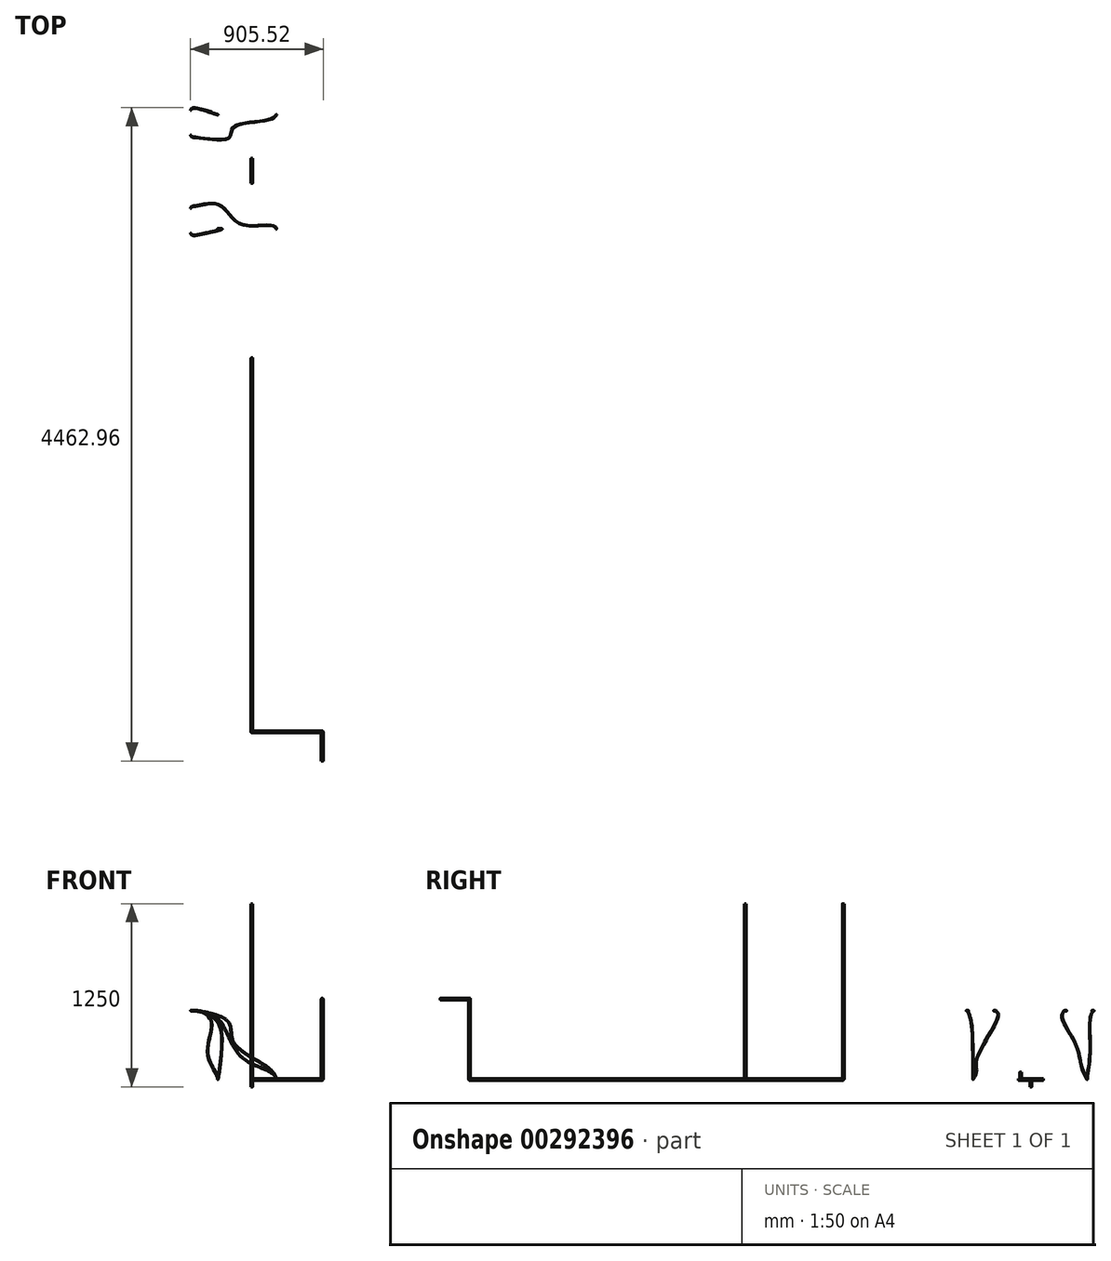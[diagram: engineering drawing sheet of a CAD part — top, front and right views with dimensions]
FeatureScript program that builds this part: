
annotation { "Feature Type Name" : "Feature", "Feature Type Description" : "" }
export const myFeature = defineFeature(function(context is Context, id is Id, definition is map)
    precondition{}
    {
        {
            var Q0;
            Q0=qCreatedBy(makeId("Front.planeOp"),FACE);
            var sketch = newSketch(context, id + "F0", { "sketchPlane" : qUnion([Q0])});
            skCircle(sketch, "E0", {"center": v(0, 0) * mm, "radius": 6.35 * mm});
            skSolve(sketch);
        }
        {
            var Q0;
            Q0 = qSketchRegion(id + "F0", true);
            extrude(context, id + "F1", {"entities" : qUnion([Q0]), "depth" : 2550 * mm});
        }
        {
            var Q0;
            Q0=qCreatedBy(makeId("Top.planeOp"),FACE);
            var sketch = newSketch(context, id + "F2", { "sketchPlane" : qUnion([Q0])});
            skLineSegment(sketch, "E1", {"start": v(0, 0) * mm, "end": v(0, -1880) * mm, "construction": true});
            skLineSegment(sketch, "E2", {"start": v(0, -1880) * mm, "end": v(0, -2550) * mm, "construction": true});
            skCircle(sketch, "E3", {"center": v(0, -1880) * mm, "radius": 6.35 * mm});
            skCircle(sketch, "E4", {"center": v(0, -2550) * mm, "radius": 6.35 * mm});
            skSolve(sketch);
        }
        {
            var Q0;
            Q0 = qSketchRegion(id + "F2", true);
            extrude(context, id + "F3", {"entities" : qUnion([Q0]), "operationType" : NewBodyOperationType.ADD, "depth" : 1200 * mm});
        }
        {
            var Q0;
            Q0=makeQuery(id+"F1.opExtrude","SWEPT_BODY",BODY,{"disambiguationData":[OSD([sQuery(id+"F0.wireOp",EDGE,"E0")])]});
            var Q1;
            Q1=makeQuery(id+"F3.opExtrude","SWEPT_FACE",FACE,{"disambiguationData":[OSD([sQuery(id+"F2.wireOp",EDGE,"E3")])]});
            transform(context, id + "F4", {"entities" : qUnion([Q0]), "transformType" : TransformType.ROTATION, "transformAxis" : qUnion([Q1]), "angle" : 180 * degree, "makeCopy" : false});
        }
        {
            var Q0;
            Q0=qCreatedBy(makeId("Top.planeOp"),FACE);
            var sketch = newSketch(context, id + "F5", { "sketchPlane" : qUnion([Q0])});
            skCircle(sketch, "E5", {"center": v(0, 0) * mm, "radius": 6.35 * mm});
            skSolve(sketch);
        }
        {
            var Q0;
            Q0 = qSketchRegion(id + "F5", true);
            extrude(context, id + "F6", {"entities" : qUnion([Q0]), "depth" : 50 * mm});
        }
        {
            var Q0;
            Q0=qCreatedBy(makeId("Top.planeOp"),FACE);
            var sketch = newSketch(context, id + "F7", { "sketchPlane" : qUnion([Q0])});
            skCircle(sketch, "E6", {"center": v(0, 71.05) * mm, "radius": 6.35 * mm});
            skLineSegment(sketch, "E7", {"start": v(0, 64.7) * mm, "end": v(0, 77.4) * mm, "construction": true});
            skLineSegment(sketch, "E8", {"start": v(-6.35, 71.05) * mm, "end": v(6.35, 71.05) * mm, "construction": true});
            skSolve(sketch);
        }
        {
            var Q0;
            Q0 = qSketchRegion(id + "F7", true);
            extrude(context, id + "F8", {"entities" : qUnion([Q0]), "oppositeDirection" : true, "depth" : 50 * mm});
        }
        {
            var Q0;
            Q0=sQuery(id+"F7.wireOp",EDGE,"E8");
            cPlane(context, id + "F9", {"entities" : qUnion([Q0]), "cplaneType" : CPlaneType.LINE_ANGLE, "offset" : 25 * mm, "angle" : 0 * degree, "width" : 150 * mm, "height" : 150 * mm});
        }
        {
            var Q0;
            Q0=qCreatedBy(id+"F9.planeOp",FACE);
            var sketch = newSketch(context, id + "F10", { "sketchPlane" : qUnion([Q0])});
            skCircle(sketch, "E9", {"center": v(0, 0) * mm, "radius": 6.35 * mm});
            skSolve(sketch);
        }
        {
            var Q0;
            Q0 = qSketchRegion(id + "F10", true);
            extrude(context, id + "F11", {"entities" : qUnion([Q0]), "operationType" : NewBodyOperationType.ADD, "endBound" : BoundingType.SYMMETRIC, "depth" : 170 * mm});
        }
        {
            var Q0;
            Q0=qCreatedBy(makeId("Top.planeOp"),FACE);
            cPlane(context, id + "F12", {"entities" : qUnion([Q0]), "cplaneType" : CPlaneType.OFFSET, "offset" : 470 * mm, "width" : 150 * mm, "height" : 150 * mm});
        }
        {
            var Q0;
            Q0=qCreatedBy(makeId("Top.planeOp"),FACE);
            var sketch = newSketch(context, id + "F13", { "sketchPlane" : qUnion([Q0])});
            skCircle(sketch, "E10", {"center": v(166.67, -325) * mm, "radius": 6.35 * mm});
            skCircle(sketch, "E11.0.1.0", {"center": v(166.67, 455) * mm, "radius": 6.35 * mm});
            skCircle(sketch, "E11.1.0.0", {"center": v(-233.33, -325) * mm, "radius": 6.35 * mm});
            skCircle(sketch, "E11.1.1.0", {"center": v(-233.33, 455) * mm, "radius": 6.35 * mm});
            skLineSegment(sketch, "E11.direction1", {"start": v(166.67, -325) * mm, "end": v(-233.33, -325) * mm, "construction": true});
            skLineSegment(sketch, "E11.direction2", {"start": v(166.67, -325) * mm, "end": v(166.67, 455) * mm, "construction": true});
            skSolve(sketch);
        }
        {
            var Q0;
            Q0=qCreatedBy(id+"F12.planeOp",FACE);
            var sketch = newSketch(context, id + "F14", { "sketchPlane" : qUnion([Q0])});
            skLineSegment(sketch, "E12", {"start": v(166.67, -325) * mm, "end": v(416.67, -325) * mm, "construction": true});
            skLineSegment(sketch, "E13", {"start": v(416.67, -354.52) * mm, "end": v(416.67, -325) * mm, "construction": true});
            skLineSegment(sketch, "E14", {"start": v(416.67, -354.52) * mm, "end": v(416.67, -269.52) * mm, "construction": true});
            skLineSegment(sketch, "E15", {"start": v(416.67, -269.52) * mm, "end": v(416.67, -184.52) * mm, "construction": true});
            skLineSegment(sketch, "E16", {"start": v(416.67, -184.52) * mm, "end": v(416.67, 400.48) * mm, "construction": true});
            skLineSegment(sketch, "E17", {"start": v(416.67, -325) * mm, "end": v(416.67, -384.52) * mm, "construction": true});
            skLineSegment(sketch, "E18", {"start": v(416.67, 400.48) * mm, "end": v(416.67, 315.48) * mm, "construction": true});
            skLineSegment(sketch, "E19", {"start": v(416.67, 400.48) * mm, "end": v(416.67, 485.48) * mm, "construction": true});
            skLineSegment(sketch, "E20.MirrorCS", {"start": v(-416.67, -354.52) * mm, "end": v(-416.67, -325) * mm, "construction": true});
            skLineSegment(sketch, "E21.MirrorCS", {"start": v(-416.67, -354.52) * mm, "end": v(-416.67, -269.52) * mm, "construction": true});
            skLineSegment(sketch, "E22.MirrorCS", {"start": v(-416.67, -325) * mm, "end": v(-416.67, -384.52) * mm, "construction": true});
            skLineSegment(sketch, "E23.MirrorCS", {"start": v(-166.67, -325) * mm, "end": v(-416.67, -325) * mm, "construction": true});
            skLineSegment(sketch, "E24.MirrorCS", {"start": v(-416.67, 400.48) * mm, "end": v(-416.67, 315.48) * mm, "construction": true});
            skLineSegment(sketch, "E25.MirrorCS", {"start": v(-416.67, 400.48) * mm, "end": v(-416.67, 485.48) * mm, "construction": true});
            skLineSegment(sketch, "E26.MirrorCS", {"start": v(-416.67, -269.52) * mm, "end": v(-416.67, -184.52) * mm, "construction": true});
            skLineSegment(sketch, "E27.MirrorCS", {"start": v(-416.67, -184.52) * mm, "end": v(-416.67, 400.48) * mm, "construction": true});
            skLineSegment(sketch, "E28", {"start": v(-416.67, -354.52) * mm, "end": v(-416.67, -369.52) * mm, "construction": true});
            skLineSegment(sketch, "E29", {"start": v(-416.67, -369.52) * mm, "end": v(-386.67, -369.52) * mm, "construction": true});
            skFitSpline(sketch, "E30", {"points": [v(-416.67, -354.52) * mm, v(-408.86, -366.73) * mm, v(-386.67, -369.52) * mm], "startDerivative": vector(0.34, -26.82) * mm, "endDerivative": vector(29.3, -3.47) * mm});
            skLineSegment(sketch, "E31", {"start": v(-416.67, -269.52) * mm, "end": v(-293.51, -269.52) * mm, "construction": true});
            skFitSpline(sketch, "E32.MirrorCS", {"points": [v(-416.67, -184.52) * mm, v(-408.86, -172.31) * mm, v(-386.67, -169.52) * mm], "startDerivative": vector(0.34, 26.82) * mm, "endDerivative": vector(29.3, 3.47) * mm});
            skLineSegment(sketch, "E33", {"start": v(-416.67, -184.52) * mm, "end": v(-416.67, 65.48) * mm, "construction": true});
            skLineSegment(sketch, "E34", {"start": v(-416.67, 65.48) * mm, "end": v(-295.06, 65.48) * mm, "construction": true});
            skFitSpline(sketch, "E35.MirrorCS", {"points": [v(-416.67, 315.48) * mm, v(-408.86, 303.27) * mm, v(-386.67, 300.48) * mm], "startDerivative": vector(0.34, -26.82) * mm, "endDerivative": vector(29.3, -3.47) * mm});
            skLineSegment(sketch, "E36", {"start": v(-416.67, 400.48) * mm, "end": v(-299.7, 400.48) * mm, "construction": true});
            skFitSpline(sketch, "E37.MirrorCS", {"points": [v(-416.67, 485.48) * mm, v(-408.86, 497.69) * mm, v(-386.67, 500.48) * mm], "startDerivative": vector(0.34, 26.82) * mm, "endDerivative": vector(29.3, 3.47) * mm});
            skLineSegment(sketch, "E38", {"start": v(-416.67, -354.52) * mm, "end": v(-309.5, -354.52) * mm});
            skLineSegment(sketch, "E39", {"start": v(-416.67, -184.52) * mm, "end": v(-206.18, -184.52) * mm});
            skLineSegment(sketch, "E40", {"start": v(-416.67, 315.48) * mm, "end": v(-297.33, 315.48) * mm});
            skLineSegment(sketch, "E41", {"start": v(-416.67, 485.48) * mm, "end": v(-294.97, 485.48) * mm});
            skSolve(sketch);
        }
        {
            var Q0;
            Q0=sQuery(id+"F14.wireOp",EDGE,"E38");
            cPlane(context, id + "F15", {"entities" : qUnion([Q0]), "cplaneType" : CPlaneType.LINE_ANGLE, "offset" : 25 * mm, "angle" : 0 * degree, "width" : 150 * mm, "height" : 150 * mm});
        }
        {
            var Q0;
            Q0=qCreatedBy(id+"F15.planeOp",FACE);
            var sketch = newSketch(context, id + "F16", { "sketchPlane" : qUnion([Q0])});
            skCircle(sketch, "E42", {"center": v(416.67, 470) * mm, "radius": 2.5 * mm});
            skSolve(sketch);
        }
        {
            var Q0;
            Q0=sQuery(id+"F14.wireOp",EDGE,"E39");
            cPlane(context, id + "F17", {"entities" : qUnion([Q0]), "cplaneType" : CPlaneType.LINE_ANGLE, "offset" : 25 * mm, "angle" : 0 * degree, "width" : 150 * mm, "height" : 150 * mm});
        }
        {
            var Q0;
            Q0=qCreatedBy(id+"F17.planeOp",FACE);
            var sketch = newSketch(context, id + "F18", { "sketchPlane" : qUnion([Q0])});
            skCircle(sketch, "E43", {"center": v(416.67, 470) * mm, "radius": 2.5 * mm});
            skSolve(sketch);
        }
        {
            var Q0;
            Q0=sQuery(id+"F14.wireOp",EDGE,"E40");
            cPlane(context, id + "F19", {"entities" : qUnion([Q0]), "cplaneType" : CPlaneType.LINE_ANGLE, "offset" : 25 * mm, "angle" : 0 * degree, "width" : 150 * mm, "height" : 150 * mm});
        }
        {
            var Q0;
            Q0=qCreatedBy(id+"F19.planeOp",FACE);
            var sketch = newSketch(context, id + "F20", { "sketchPlane" : qUnion([Q0])});
            skCircle(sketch, "E44", {"center": v(416.67, 470) * mm, "radius": 2.5 * mm});
            skSolve(sketch);
        }
        {
            var Q0;
            Q0=sQuery(id+"F14.wireOp",EDGE,"E41");
            cPlane(context, id + "F21", {"entities" : qUnion([Q0]), "cplaneType" : CPlaneType.LINE_ANGLE, "offset" : 25 * mm, "angle" : 0 * degree, "width" : 150 * mm, "height" : 150 * mm});
        }
        {
            var Q0;
            Q0=qCreatedBy(id+"F21.planeOp",FACE);
            var sketch = newSketch(context, id + "F22", { "sketchPlane" : qUnion([Q0])});
            skCircle(sketch, "E45", {"center": v(416.67, 470) * mm, "radius": 2.5 * mm});
            skSolve(sketch);
        }
        {
            var Q0;
            Q0=makeQuery(id+"F22.imprint","IMPRINT",FACE,{"disambiguationData":[TD([[makeQuery(id+"F22.imprint","IMPRINT",EDGE,{"derivedFrom":sQuery(id+"F22.wireOp",EDGE,"E45")}),1.0]])]});
            var Q1;
            Q1=sQuery(id+"F14.wireOp",EDGE,"E37.MirrorCS");
            sweep(context, id + "F23", {"profiles" : qUnion([Q0]), "path" : qUnion([Q1])});
        }
        {
            var Q0;
            Q0=makeQuery(id+"F20.imprint","IMPRINT",FACE,{"disambiguationData":[TD([[makeQuery(id+"F20.imprint","IMPRINT",EDGE,{"derivedFrom":sQuery(id+"F20.wireOp",EDGE,"E44")}),1.0]])]});
            var Q1;
            Q1=sQuery(id+"F20.wireOp",EDGE,"E44");
            var Q2;
            Q2=sQuery(id+"F14.wireOp",EDGE,"E35.MirrorCS");
            sweep(context, id + "F24", {"profiles" : qUnion([Q0]), "surfaceProfiles" : qUnion([Q1]), "path" : qUnion([Q2])});
        }
        {
            var Q0;
            Q0=makeQuery(id+"F18.imprint","IMPRINT",FACE,{"disambiguationData":[TD([[makeQuery(id+"F18.imprint","IMPRINT",EDGE,{"derivedFrom":sQuery(id+"F18.wireOp",EDGE,"E43")}),1.0]])]});
            var Q1;
            Q1=sQuery(id+"F14.wireOp",EDGE,"E32.MirrorCS");
            sweep(context, id + "F25", {"profiles" : qUnion([Q0]), "path" : qUnion([Q1])});
        }
        {
            var Q0;
            Q0=makeQuery(id+"F16.imprint","IMPRINT",FACE,{"disambiguationData":[TD([[makeQuery(id+"F16.imprint","IMPRINT",EDGE,{"derivedFrom":sQuery(id+"F16.wireOp",EDGE,"E42")}),1.0]])]});
            var Q1;
            Q1=sQuery(id+"F16.wireOp",EDGE,"E42");
            var Q2;
            Q2=sQuery(id+"F14.wireOp",EDGE,"E30");
            sweep(context, id + "F26", {"profiles" : qUnion([Q0]), "surfaceProfiles" : qUnion([Q1]), "path" : qUnion([Q2])});
        }
        {
            var Q0;
            Q0=sQuery(id+"F14.wireOp",VERTEX,"E29.end");
            var Q1;
            Q1=sQuery(id+"F13.wireOp",VERTEX,"E11.1.0.0.center");
            var Q2;
            Q2=sQuery(id+"F14.wireOp",VERTEX,"E23.MirrorCS.start");
            cPlane(context, id + "F27", {"entities" : qUnion([Q0, Q1, Q2]), "cplaneType" : CPlaneType.THREE_POINT, "offset" : 25 * mm, "width" : 150 * mm, "height" : 150 * mm});
        }
        {
            var Q0;
            Q0=qCreatedBy(id+"F27.planeOp",FACE);
            var sketch = newSketch(context, id + "F28", { "sketchPlane" : qUnion([Q0])});
            skPoint(sketch, "E46", {"position": v(449.55, 480.4) * mm});
            skPoint(sketch, "E47", {"position": v(293.11, 9.32) * mm});
            skFitSpline(sketch, "E48", {"points": [v(449.55, 480.4) * mm, v(350.75, 449.89) * mm, v(269.3, 340.3) * mm, v(293.11, 9.32) * mm], "startDerivative": vector(-540.37, -2.95) * mm, "endDerivative": vector(33.47, -166.56) * mm});
            skSolve(sketch);
        }
        {
            var Q0;
            Q0=makeQuery(id+"F26.opSweep","CAP_FACE",FACE,{"disambiguationData":[OSD([sQuery(id+"F14.wireOp",VERTEX,"E30.end"),sQuery(id+"F16.wireOp",EDGE,"E42")])],"isStart":false});
            var Q1;
            Q1=sQuery(id+"F28.wireOp",EDGE,"E48");
            sweep(context, id + "F29", {"operationType" : NewBodyOperationType.ADD, "profiles" : qUnion([Q0]), "path" : qUnion([Q1])});
        }
        {
            var Q0;
            Q0=makeQuery(id+"F13.imprint","IMPRINT",FACE,{"disambiguationData":[TD([[makeQuery(id+"F13.imprint","IMPRINT",EDGE,{"derivedFrom":sQuery(id+"F13.wireOp",EDGE,"E11.1.0.0")}),1.0]])]});
            var Q1;
            Q1=sQuery(id+"F13.wireOp",EDGE,"E11.1.0.0");
            extrude(context, id + "F30", {"entities" : qUnion([Q0]), "operationType" : NewBodyOperationType.REMOVE, "surfaceEntities" : qUnion([Q1]), "endBound" : BoundingType.SYMMETRIC, "oppositeDirection" : true, "depth" : 5 * mm});
        }
        {
            var Q0;
            Q0=sQuery(id+"F14.wireOp",EDGE,"E16");
            cPoint(context, id + "F31", {"entities" : qUnion([Q0]), "parameter" : 0.5});
        }
        {
            var Q0;
            Q0=sQuery(id+"F14.wireOp",VERTEX,"E32.MirrorCS.2.internal");
            var Q1;
            Q1=sQuery(id+"F13.wireOp",VERTEX,"E10.center");
            var Q2;
            Q2 = qCreatedBy(id + "F31" ,VERTEX);
            cPlane(context, id + "F32", {"entities" : qUnion([Q0, Q1, Q2]), "cplaneType" : CPlaneType.THREE_POINT, "offset" : 25 * mm, "width" : 150 * mm, "height" : 150 * mm});
        }
        {
            var Q0;
            Q0=qCreatedBy(id+"F32.planeOp",FACE);
            var sketch = newSketch(context, id + "F33", { "sketchPlane" : qUnion([Q0])});
            skPoint(sketch, "E49", {"position": v(483.8, 277.64) * mm});
            skPoint(sketch, "E50", {"position": v(-90.52, -192.9) * mm});
            skFitSpline(sketch, "E51", {"points": [v(483.8, 277.64) * mm, v(320.18, 237.44) * mm, v(137.24, -66.8) * mm, v(-90.52, -192.9) * mm], "startDerivative": vector(-588.21, -32.32) * mm, "endDerivative": vector(-68.51, -732.15) * mm});
            skSolve(sketch);
        }
        {
            var Q0;
            Q0=makeQuery(id+"F25.opSweep","CAP_FACE",FACE,{"disambiguationData":[OSD([sQuery(id+"F14.wireOp",VERTEX,"E32.MirrorCS.end"),sQuery(id+"F18.wireOp",EDGE,"E43")])],"isStart":false});
            var Q1;
            Q1=sQuery(id+"F33.wireOp",EDGE,"E51");
            sweep(context, id + "F34", {"operationType" : NewBodyOperationType.ADD, "profiles" : qUnion([Q0]), "path" : qUnion([Q1])});
        }
        {
            var Q0;
            Q0=sQuery(id+"F14.wireOp",EDGE,"E16");
            cPoint(context, id + "F35", {"entities" : qUnion([Q0]), "parameter" : 0.5});
        }
        {
            var Q0;
            Q0=sQuery(id+"F14.wireOp",VERTEX,"E35.MirrorCS.end");
            var Q1;
            Q1=sQuery(id+"F13.wireOp",VERTEX,"E11.0.1.0.center");
            var Q2;
            Q2 = qCreatedBy(id + "F35" ,VERTEX);
            cPlane(context, id + "F36", {"entities" : qUnion([Q0, Q1, Q2]), "cplaneType" : CPlaneType.THREE_POINT, "offset" : 25 * mm, "width" : 150 * mm, "height" : 150 * mm});
        }
        {
            var Q0;
            Q0=qCreatedBy(id+"F36.planeOp",FACE);
            var sketch = newSketch(context, id + "F37", { "sketchPlane" : qUnion([Q0])});
            skPoint(sketch, "E52", {"position": v(479.29, 244.44) * mm});
            skPoint(sketch, "E53", {"position": v(-85.5, -237.2) * mm});
            skFitSpline(sketch, "E54", {"points": [v(479.29, 244.44) * mm, v(259.93, 193.97) * mm, v(212.44, 24) * mm, v(-17.53, -142.24) * mm, v(-85.5, -237.2) * mm], "startDerivative": vector(-296.58, -3.1) * mm, "endDerivative": vector(-86.75, -534.76) * mm});
            skSolve(sketch);
        }
        {
            var Q0;
            Q0=makeQuery(id+"F24.opSweep","CAP_FACE",FACE,{"disambiguationData":[OSD([sQuery(id+"F14.wireOp",VERTEX,"E35.MirrorCS.end"),sQuery(id+"F20.wireOp",EDGE,"E44")])],"isStart":false});
            var Q1;
            Q1=sQuery(id+"F37.wireOp",EDGE,"E54");
            sweep(context, id + "F38", {"operationType" : NewBodyOperationType.ADD, "profiles" : qUnion([Q0]), "path" : qUnion([Q1])});
        }
        {
            var Q0;
            Q0=sQuery(id+"F14.wireOp",VERTEX,"E37.MirrorCS.2.internal");
            var Q1;
            Q1=sQuery(id+"F13.wireOp",VERTEX,"E11.1.1.0.center");
            var Q2;
            Q2=sQuery(id+"F14.wireOp",VERTEX,"E18.end");
            cPlane(context, id + "F39", {"entities" : qUnion([Q0, Q1, Q2]), "cplaneType" : CPlaneType.THREE_POINT, "offset" : 25 * mm, "width" : 150 * mm, "height" : 150 * mm});
        }
        {
            var Q0;
            Q0=qCreatedBy(id+"F39.planeOp",FACE);
            var sketch = newSketch(context, id + "F40", { "sketchPlane" : qUnion([Q0])});
            skPoint(sketch, "E55", {"position": v(486.8, 480.72) * mm});
            skPoint(sketch, "E56", {"position": v(329.45, 9.84) * mm});
            skFitSpline(sketch, "E57", {"points": [v(486.8, 480.72) * mm, v(372.4, 399.14) * mm, v(398.78, 179.82) * mm, v(329.45, 9.84) * mm], "startDerivative": vector(-566.02, -21.9) * mm, "endDerivative": vector(56.77, -259.14) * mm});
            skSolve(sketch);
        }
        {
            var Q0;
            Q0=makeQuery(id+"F23.opSweep","CAP_FACE",FACE,{"disambiguationData":[OSD([sQuery(id+"F14.wireOp",VERTEX,"E37.MirrorCS.end"),sQuery(id+"F22.wireOp",EDGE,"E45")])],"isStart":false});
            var Q1;
            Q1=sQuery(id+"F40.wireOp",EDGE,"E57");
            sweep(context, id + "F41", {"operationType" : NewBodyOperationType.ADD, "profiles" : qUnion([Q0]), "path" : qUnion([Q1])});
        }
        {
            var Q0;
            Q0=makeQuery(id+"F1.opExtrude","CAP_FACE",FACE,{"disambiguationData":[OSD([sQuery(id+"F0.wireOp",EDGE,"E0")])],"isStart":true});
            var sketch = newSketch(context, id + "F42", { "sketchPlane" : qUnion([Q0])});
            skLineSegment(sketch, "E58", {"start": v(0, 6.35) * mm, "end": v(0, -6.35) * mm});
            skPoint(sketch, "E59", {"position": v(0, 0) * mm});
            skSolve(sketch);
        }
        {
            var Q0;
            Q0=sQuery(id+"F42.wireOp",EDGE,"E58");
            cPlane(context, id + "F43", {"entities" : qUnion([Q0]), "cplaneType" : CPlaneType.LINE_ANGLE, "offset" : 25 * mm, "angle" : 0 * degree, "width" : 150 * mm, "height" : 150 * mm});
        }
        {
            var Q0;
            Q0=qCreatedBy(id+"F43.planeOp",FACE);
            var sketch = newSketch(context, id + "F44", { "sketchPlane" : qUnion([Q0])});
            skCircle(sketch, "E60", {"center": v(3760, 0) * mm, "radius": 6.35 * mm});
            skSolve(sketch);
        }
        {
            var Q0;
            {var subQ0=sQuery(id+"F42.wireOp",EDGE,"E58");Q0=makeQuery(id+"F42.imprint","IMPRINT",FACE,{"disambiguationData":[TD([[makeQuery(id+"F42.imprint","IMPRINT",EDGE,{"derivedFrom":subQ0}),-1.0]])]});}
            cPlane(context, id + "F45", {"entities" : qUnion([Q0]), "cplaneType" : CPlaneType.OFFSET, "offset" : 0 * mm, "width" : 150 * mm, "height" : 150 * mm});
        }
        {
            var Q0;
            Q0=qCreatedBy(id+"F45.planeOp",FACE);
            var sketch = newSketch(context, id + "F46", { "sketchPlane" : qUnion([Q0])});
            skLineSegment(sketch, "E61", {"start": v(0, 0) * mm, "end": v(480, 0) * mm});
            skLineSegment(sketch, "E62", {"start": v(480, 0) * mm, "end": v(480, 550) * mm});
            skSolve(sketch);
        }
        {
            var Q0;
            Q0=makeQuery(id+"F44.imprint","IMPRINT",FACE,{"disambiguationData":[TD([[makeQuery(id+"F44.imprint","IMPRINT",EDGE,{"derivedFrom":sQuery(id+"F44.wireOp",EDGE,"E60")}),1.0]])]});
            var Q1;
            Q1=sQuery(id+"F44.wireOp",EDGE,"E60");
            extrude(context, id + "F47", {"entities" : qUnion([Q0]), "operationType" : NewBodyOperationType.ADD, "surfaceEntities" : qUnion([Q1]), "oppositeDirection" : true, "depth" : 480 * mm});
        }
        {
            var Q0;
            Q0=makeQuery(id+"F47.opExtrude","CAP_FACE",FACE,{"disambiguationData":[OSD([sQuery(id+"F44.wireOp",EDGE,"E60")])],"isStart":false});
            var sketch = newSketch(context, id + "F48", { "sketchPlane" : qUnion([Q0])});
            skLineSegment(sketch, "E63", {"start": v(-3753.65, 0) * mm, "end": v(-3766.35, 0) * mm});
            skSolve(sketch);
        }
        {
            var Q0;
            {var subQ0=sQuery(id+"F42.wireOp",EDGE,"E58");Q0=makeQuery(id+"F42.imprint","IMPRINT",FACE,{"disambiguationData":[TD([[makeQuery(id+"F42.imprint","IMPRINT",EDGE,{"derivedFrom":subQ0}),-1.0]])]});}
            var Q1;
            Q1=makeQuery(id+"F1.opExtrude","CAP_EDGE",EDGE,{"disambiguationData":[OSD([sQuery(id+"F0.wireOp",EDGE,"E0")])],"isStart":true});
            var Q2;
            Q2=sQuery(id+"F42.wireOp",EDGE,"E58");
            revolve(context, id + "F49", {"operationType" : NewBodyOperationType.ADD, "entities" : qUnion([Q0]), "surfaceEntities" : qUnion([Q1]), "axis" : qUnion([Q2]), "revolveType" : RevolveType.ONE_DIRECTION, "oppositeDirection" : true, "angle" : 90 * degree});
        }
        {
            var Q0;
            Q0=sQuery(id+"F48.wireOp",EDGE,"E63");
            cPlane(context, id + "F50", {"entities" : qUnion([Q0]), "cplaneType" : CPlaneType.LINE_ANGLE, "offset" : 25 * mm, "angle" : 0 * degree, "width" : 150 * mm, "height" : 150 * mm});
        }
        {
            var Q0;
            Q0=qCreatedBy(id+"F50.planeOp",FACE);
            var sketch = newSketch(context, id + "F51", { "sketchPlane" : qUnion([Q0])});
            skCircle(sketch, "E64", {"center": v(480, 3760) * mm, "radius": 6.35 * mm});
            skSolve(sketch);
        }
        {
            var Q0;
            Q0 = qSketchRegion(id + "F51", true);
            extrude(context, id + "F52", {"entities" : qUnion([Q0]), "operationType" : NewBodyOperationType.ADD, "oppositeDirection" : true, "depth" : 550 * mm});
        }
        {
            var Q0;
            {var subQ0=sQuery(id+"F48.wireOp",EDGE,"E63");Q0=makeQuery(id+"F48.imprint","IMPRINT",FACE,{"disambiguationData":[TD([[makeQuery(id+"F48.imprint","IMPRINT",EDGE,{"derivedFrom":subQ0}),1.0]])]});}
            var Q1;
            Q1=makeQuery(id+"F47.opExtrude","CAP_EDGE",EDGE,{"disambiguationData":[OSD([sQuery(id+"F44.wireOp",EDGE,"E60")])],"isStart":false});
            var Q2;
            Q2=sQuery(id+"F48.wireOp",EDGE,"E63");
            revolve(context, id + "F53", {"operationType" : NewBodyOperationType.ADD, "entities" : qUnion([Q0]), "surfaceEntities" : qUnion([Q1]), "axis" : qUnion([Q2]), "revolveType" : RevolveType.FULL});
        }
        {
            var Q0;
            Q0=makeQuery(id+"F52.opExtrude","CAP_FACE",FACE,{"disambiguationData":[OSD([sQuery(id+"F51.wireOp",EDGE,"E64")])],"isStart":false});
            var sketch = newSketch(context, id + "F54", { "sketchPlane" : qUnion([Q0])});
            skLineSegment(sketch, "E65", {"start": v(480, -3760) * mm, "end": v(473.65, -3760) * mm});
            skLineSegment(sketch, "E66", {"start": v(473.65, -3760) * mm, "end": v(486.35, -3760) * mm});
            skSolve(sketch);
        }
        {
            var Q0;
            Q0=sQuery(id+"F54.wireOp",EDGE,"E66");
            cPlane(context, id + "F55", {"entities" : qUnion([Q0]), "cplaneType" : CPlaneType.LINE_ANGLE, "offset" : 25 * mm, "angle" : 0 * degree, "width" : 150 * mm, "height" : 150 * mm});
        }
        {
            var Q0;
            Q0=qCreatedBy(id+"F55.planeOp",FACE);
            var sketch = newSketch(context, id + "F56", { "sketchPlane" : qUnion([Q0])});
            skCircle(sketch, "E67", {"center": v(-480, 550) * mm, "radius": 6.35 * mm});
            skSolve(sketch);
        }
        {
            var Q0;
            Q0 = qSketchRegion(id + "F56", true);
            extrude(context, id + "F57", {"entities" : qUnion([Q0]), "operationType" : NewBodyOperationType.ADD, "oppositeDirection" : true, "depth" : 200 * mm});
        }
        {
            var Q0;
            {var subQ0=sQuery(id+"F54.wireOp",EDGE,"E66");var subQ3=makeQuery(id+"F54.imprint","IMPRINT",VERTEX,{"derivedFrom":subQ0});Q0=makeQuery(id+"F54.imprint","IMPRINT",FACE,{"disambiguationData":[TD([[makeQuery(id+"F54.imprint","IMPRINT",EDGE,{"disambiguationData":[TD([[subQ3,1.0]])],"derivedFrom":subQ0}),1.0]])]});}
            var Q1;
            Q1=sQuery(id+"F54.wireOp",EDGE,"E66");
            revolve(context, id + "F58", {"operationType" : NewBodyOperationType.ADD, "entities" : qUnion([Q0]), "axis" : qUnion([Q1]), "revolveType" : RevolveType.FULL});
        }
    });
